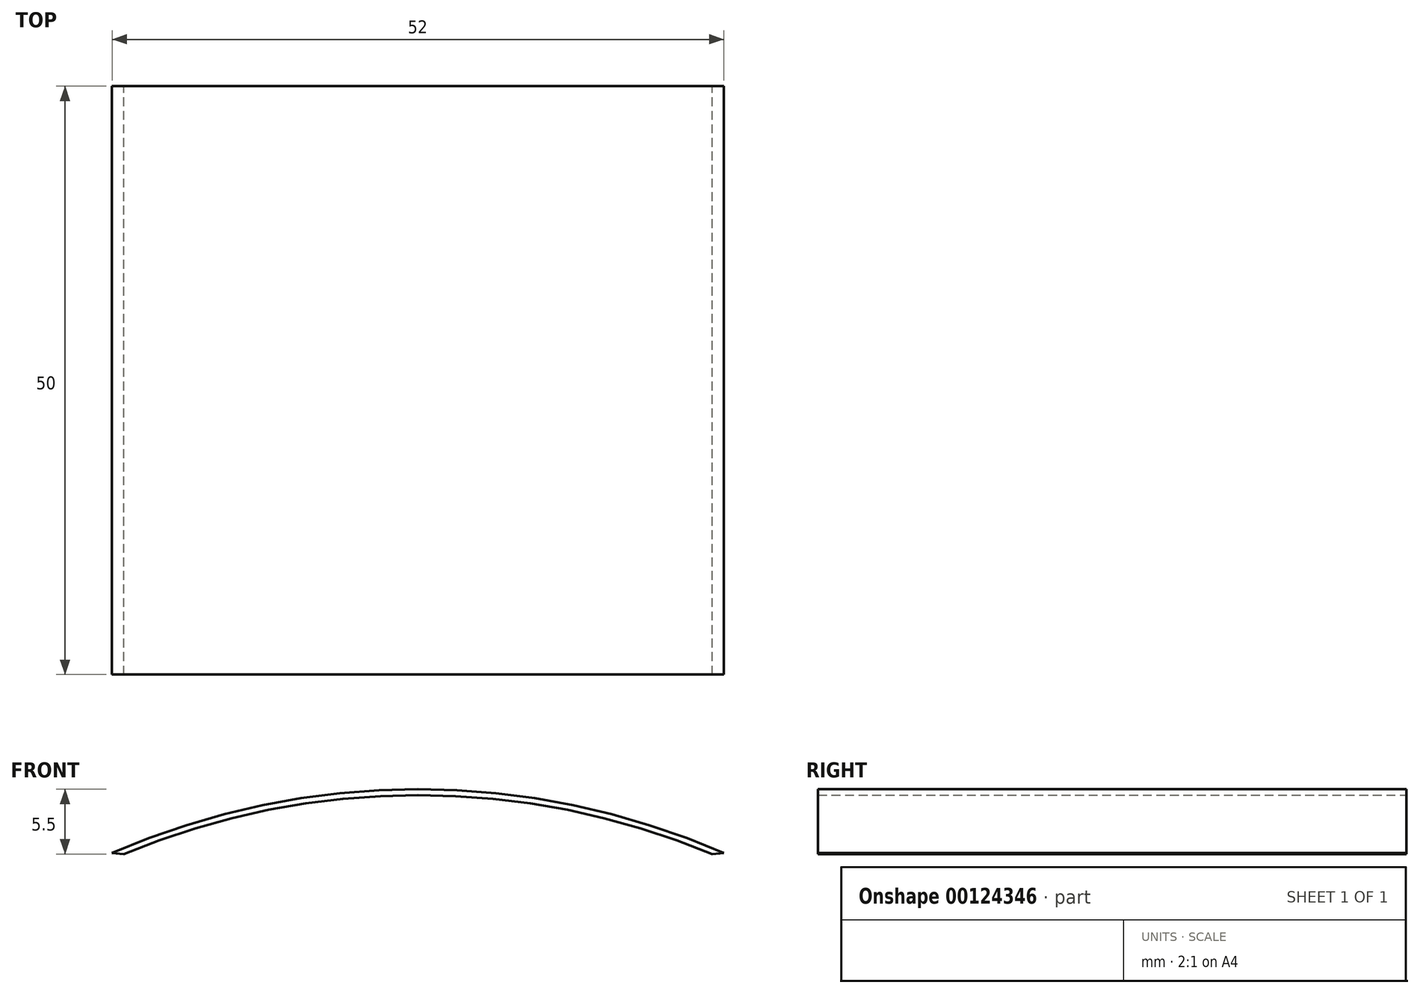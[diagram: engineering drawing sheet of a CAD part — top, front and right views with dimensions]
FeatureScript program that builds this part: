
annotation { "Feature Type Name" : "Feature", "Feature Type Description" : "" }
export const myFeature = defineFeature(function(context is Context, id is Id, definition is map)
    precondition{}
    {
        {
            var Q0;
            Q0=qCreatedBy(makeId("Front.planeOp"),FACE);
            var sketch = newSketch(context, id + "F0", { "sketchPlane" : qUnion([Q0])});
            skArc(sketch, "E0", {"start": v(25.3, 0) * mm, "mid": v(0.3, 5) * mm, "end": v(-24.7, 0) * mm});
            skArc(sketch, "E1", {"start": v(26.3, 0.07) * mm, "mid": v(0.3, 5.5) * mm, "end": v(-25.7, 0.07) * mm});
            skLineSegment(sketch, "E2", {"start": v(-25.7, 0.07) * mm, "end": v(-24.7, 0) * mm});
            skLineSegment(sketch, "E3", {"start": v(26.3, 0.07) * mm, "end": v(25.3, 0) * mm});
            skSolve(sketch);
        }
        {
            var Q0;
            Q0=makeQuery(id+"F0.imprint","IMPRINT",FACE,{"disambiguationData":[TD([[makeQuery(id+"F0.imprint","IMPRINT",EDGE,{"derivedFrom":sQuery(id+"F0.wireOp",EDGE,"E0")}),-1.0]])]});
            extrude(context, id + "F1", {"entities" : qUnion([Q0]), "depth" : 50 * mm});
        }
    });
